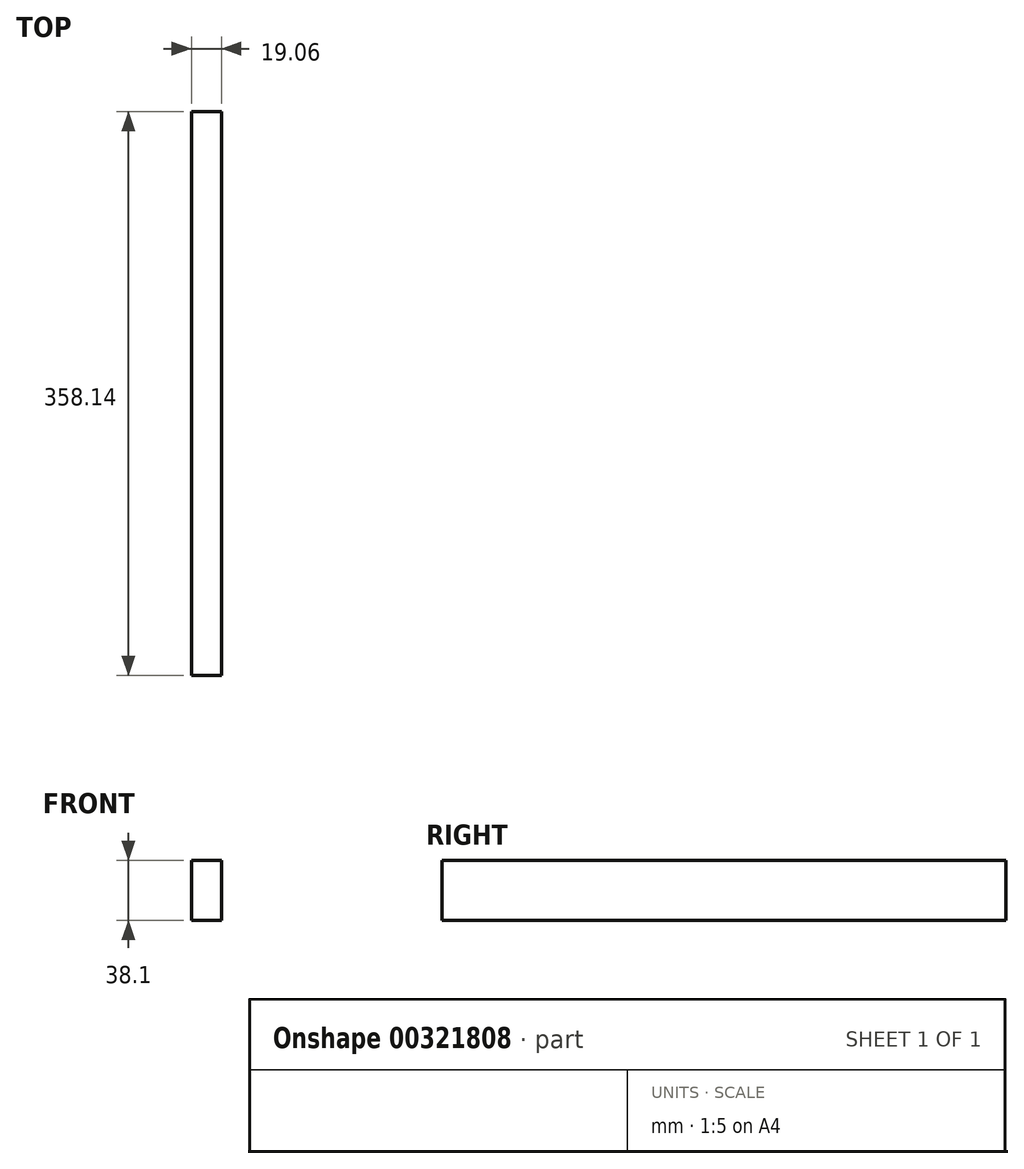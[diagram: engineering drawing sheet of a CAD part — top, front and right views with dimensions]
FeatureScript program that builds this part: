
annotation { "Feature Type Name" : "Feature", "Feature Type Description" : "" }
export const myFeature = defineFeature(function(context is Context, id is Id, definition is map)
    precondition{}
    {
        {
            var Q0;
            Q0=qCreatedBy(makeId("Front.planeOp"),FACE);
            var sketch = newSketch(context, id + "F0", { "sketchPlane" : qUnion([Q0])});
            skLineSegment(sketch, "E0.bottom", {"start": v(-9.53, 19.05) * mm, "end": v(9.53, 19.05) * mm});
            skLineSegment(sketch, "E0.top", {"start": v(-9.53, -19.05) * mm, "end": v(9.52, -19.05) * mm});
            skLineSegment(sketch, "E0.left", {"start": v(-9.52, 19.05) * mm, "end": v(-9.53, -19.05) * mm});
            skLineSegment(sketch, "E0.right", {"start": v(9.53, 19.05) * mm, "end": v(9.52, -19.05) * mm});
            skPoint(sketch, "E0.middle", {"position": v(0, 0) * mm});
            skSolve(sketch);
        }
        {
            var Q0;
            Q0=qSketchRegion(id+"F0",true);
            extrude(context, id + "F1", {"entities" : qUnion([Q0]), "endBound" : BoundingType.SYMMETRIC, "depth" : 396.24 * mm - 38.1 * mm, "offsetDistance" : 25 * mm});
        }
    });
